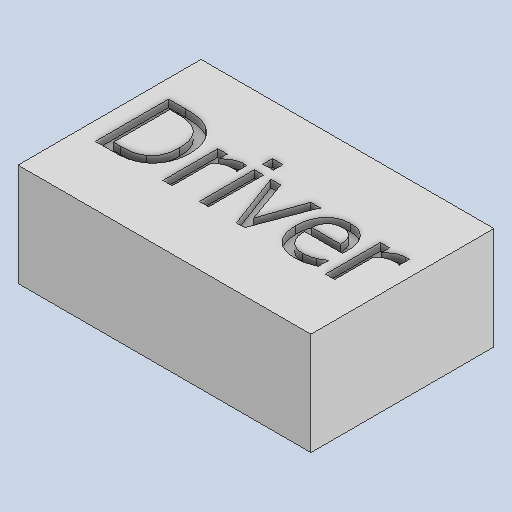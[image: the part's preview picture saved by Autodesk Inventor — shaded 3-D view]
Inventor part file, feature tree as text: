
AUTODESK INVENTOR PART (.ipt)
format: ipt  version: 2023 (Build 270158000, 158)  size: 297,472 bytes
history: native  units: in
note: dims shown in document units (in); Inventor stores cm internally (conversion verified against a paired STEP export)
features: extrude x2, sketch x2, projected_geometry x1
ambient origin geometry x8: Origin, YZ Plane, XZ Plane, XY Plane, X Axis, Y Axis, Z Axis, Center Point
bodies: Solid1 (feature_tree)
feature tree (5):
  extrude  "Extrusion1"  Depth=0.9843in
  extrude  "Extrusion2"  Depth=0.0394in TaperAngle=0.0deg
  sketch  "Sketch1"  dims[d0=1.5748in d1=0.9843in]
  sketch  "Sketch2"  dims[d2=0.5512in d3=0.0in d4=0.0394in d5=0.0in]
  projected_geometry  "Projected Loop1"
